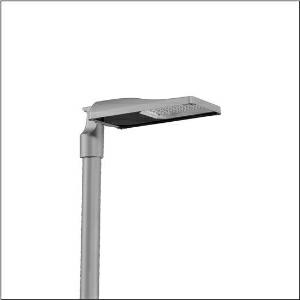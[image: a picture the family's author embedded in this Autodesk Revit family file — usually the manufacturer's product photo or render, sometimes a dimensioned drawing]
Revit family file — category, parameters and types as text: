
# Revit family: streetlight_sl_31_mini___st1_0a_5xh2d3aa08ha_083f
name_source: partatom
category: Lighting Fixtures
units: mm (PartAtom-declared; Revit-internal decimal feet)

## family parameters
Cut with Voids When Loaded = No
Host = Face
Light Source = No
Part Type = Normal
Room Calculation Point = No
Round Connector Dimension = Use Diameter
Shared = No

## types (1)
- --- (1 x LED, 9240 lm, 68.3 W, 3000K)
    Apparent Load = 68 VA
    CIE Flux Codes = 37 72 97 100 100
    Color Rendering = 70
    Color Temperature = 3000K
    Default Elevation = 1800 mm
    Description = Streetlight SL 31 mini Easy mast luminaire for post-top, side-entry; light control with lens of PMMA; light distribution: ST1.0a, direct asymmetric distribution, for standard-compliant lighting for roads and squares; LED: luminous flux: 9.240lm, light colour: 730, colour temperature: 3000K; luminous efficacy: 135,3lm/W; control: overheat protection, intelligent temperature release in ECG and LED module, constant luminous flux control, time-dependent luminous flux control, flexible luminous flux parameterisation, pre-setting: linear dimming characteristic; luminaire housing, of diecast aluminium, SITECO metallic grey (DB 702S), corrosivity category C5 high according to DIN EN ISO 12944; cover of toughened safety glass, transparent, mast flange of diecast aluminium, SITECO metallic grey (DB 702S), spigot size: 76/60mm, mast flange included unmounted; cable length: 8,5m, connection cable pre-assembled; mains connection: 220..240V, AC, 50/60Hz; power consumption (at start of service life): 68,3W / (at end of service life): 74,8W / (with reduced operation 50%): 29,7W; protection rating (complete): IP66; insulation class (complete): insulation class II (safety insulation); impact resistance: IK10; certification: CE, ENEC, ENEC+, VDE, UKCA; permissible operating ambient temperature for outdoor applications: -40..+50°C; packaging unit: 1 piece

Light Distribution: ST1.0a
    Height = 76 mm
    Lamp = 1 x LED
    Lamp Light Flux = 9240 lm
    Lamp Power = 68.3 W
    Lamp count = 1
    Length = 547 mm
    Luminous efficacy = 135 lm/W
    Manufacturer = Siteco
    ModVariant = No
    Model = 5XH2D3AA08HA
    Number of Poles = 1
    OnlyDefault = Yes
    Power Factor = 1
    Product Name = Streetlight SL 31 mini | ST1.0a
    Product group = mast luminaire | pylon top
    ProductGroupID = 6100
    Protection Class = Protection class II
    Protection Degree = IP 66
    RLX_Detail_Level = 1
    RLX_Emergency_Light_Flux = 0 lm
    RLX_Emergency_Type = 0
    RLX_Emergency_Type_DB = No
    RlxData = <blob elided: 39281 chars, md5=2d44086f>
    Socket = socket
    Standby Power = 0 W
    System Light Flux = 9240 lm
    System Power = 68 W
    Type Comments = factory setting: luminous flux: 100 % | dim-lin: 254 | 693 mA
    Type Image = l_1300326.jpg
    URL = http://relux.com
    VarID = @adj_061769
    Voltage = 0 V
    Weight = 0.00 kg
    Width = 265 mm

## geometry (parser evidence)
native form markers: Blend x4, Sweep x11
no freeform markers — native parametric forms only
